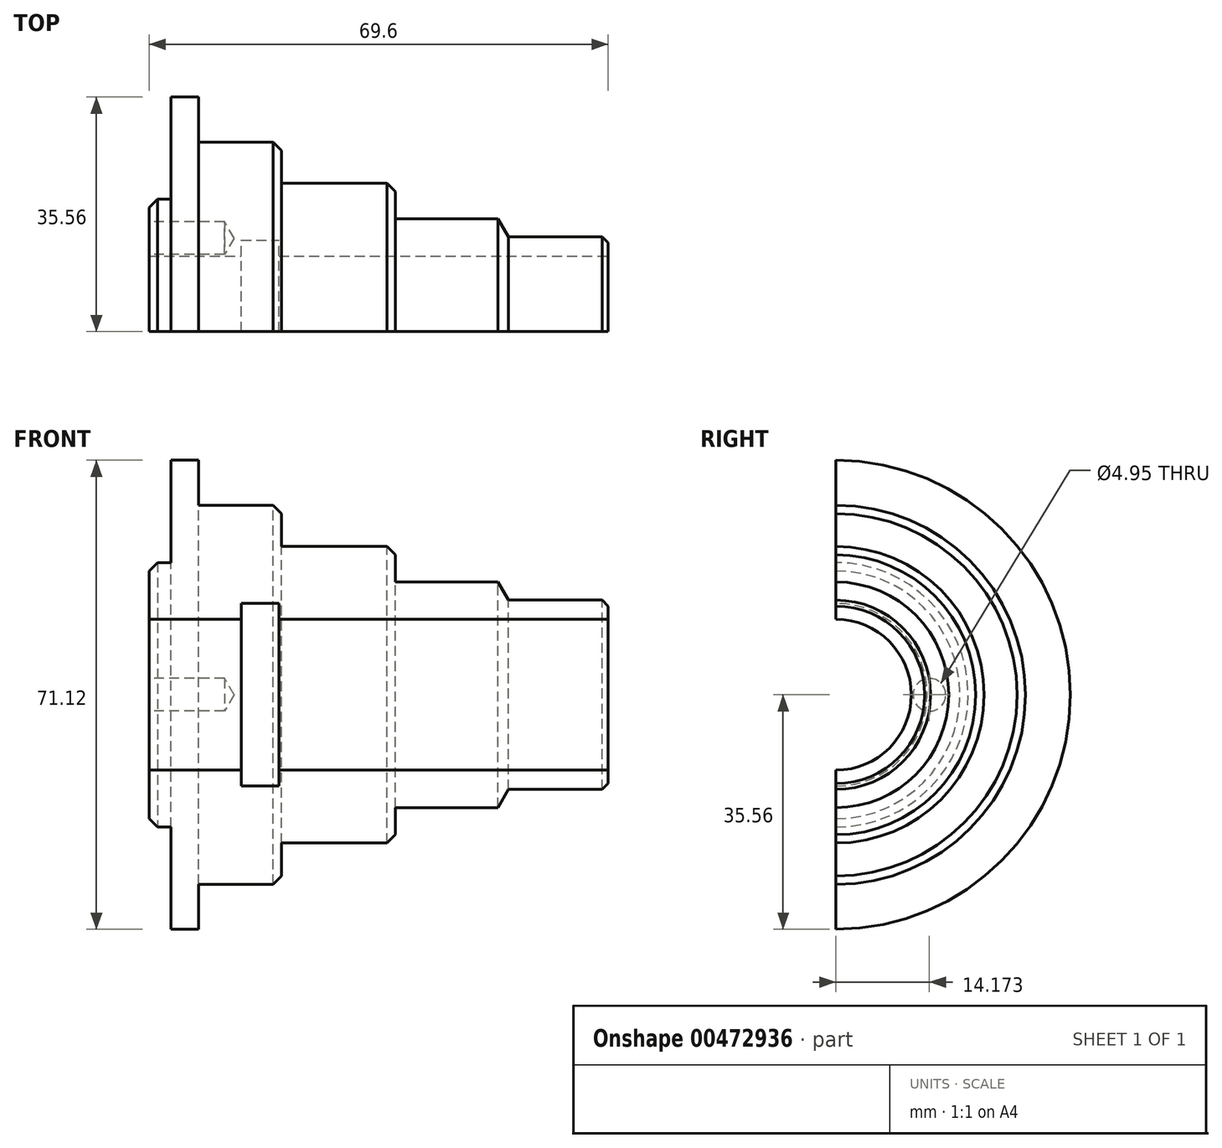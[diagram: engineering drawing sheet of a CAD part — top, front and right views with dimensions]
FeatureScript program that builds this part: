
annotation { "Feature Type Name" : "Feature", "Feature Type Description" : "" }
export const myFeature = defineFeature(function(context is Context, id is Id, definition is map)
    precondition{}
    {
        {
            var Q0;
            Q0=qCreatedBy(makeId("Front.planeOp"),FACE);
            var sketch = newSketch(context, id + "F0", { "sketchPlane" : qUnion([Q0])});
            skLineSegment(sketch, "E0", {"start": v(0, 0) * mm, "end": v(0, 11.43) * mm});
            skLineSegment(sketch, "E1", {"start": v(0, 11.43) * mm, "end": v(0, 13.45) * mm});
            skLineSegment(sketch, "E2", {"start": v(0, 13.45) * mm, "end": v(-0.9, 14.35) * mm});
            skLineSegment(sketch, "E3", {"start": v(-0.9, 14.35) * mm, "end": v(-15.12, 14.35) * mm});
            skLineSegment(sketch, "E4", {"start": v(0, 11.43) * mm, "end": v(-49.91, 11.43) * mm});
            skLineSegment(sketch, "E5", {"start": v(-15.12, 14.35) * mm, "end": v(-16.7, 17.1) * mm});
            skLineSegment(sketch, "E6", {"start": v(-16.7, 17.1) * mm, "end": v(-32.26, 17.1) * mm});
            skLineSegment(sketch, "E7", {"start": v(-32.26, 17.1) * mm, "end": v(-32.26, 22.48) * mm});
            skLineSegment(sketch, "E8", {"start": v(-32.26, 22.48) * mm, "end": v(-49.53, 22.48) * mm});
            skLineSegment(sketch, "E9", {"start": v(-49.53, 22.48) * mm, "end": v(-49.53, 28.74) * mm});
            skLineSegment(sketch, "E10", {"start": v(-49.53, 28.74) * mm, "end": v(-62.1, 28.74) * mm});
            skLineSegment(sketch, "E11", {"start": v(-62.1, 28.74) * mm, "end": v(-62.1, 35.56) * mm});
            skLineSegment(sketch, "E12", {"start": v(-62.1, 35.56) * mm, "end": v(-66.3, 35.56) * mm});
            skLineSegment(sketch, "E13", {"start": v(-66.3, 35.56) * mm, "end": v(-66.3, 20.05) * mm});
            skLineSegment(sketch, "E14", {"start": v(-66.3, 20.05) * mm, "end": v(-69.6, 20.05) * mm});
            skLineSegment(sketch, "E15", {"start": v(-69.6, 20.05) * mm, "end": v(-69.6, 11.43) * mm});
            skLineSegment(sketch, "E16", {"start": v(0, 0) * mm, "end": v(-69.06, 0) * mm});
            skLineSegment(sketch, "E17", {"start": v(-69.6, 11.43) * mm, "end": v(-55.63, 11.43) * mm});
            skLineSegment(sketch, "E18", {"start": v(-55.63, 11.43) * mm, "end": v(-55.63, 13.84) * mm});
            skLineSegment(sketch, "E19", {"start": v(-55.63, 13.84) * mm, "end": v(-49.91, 13.84) * mm});
            skLineSegment(sketch, "E20", {"start": v(-49.91, 13.84) * mm, "end": v(-49.91, 11.43) * mm});
            skLineSegment(sketch, "E21.trimOffspring", {"start": v(-55.63, 11.43) * mm, "end": v(-254, 11.43) * mm});
            skSolve(sketch);
        }
        {
            var Q0;
            Q0=makeQuery(id+"F0.imprint","IMPRINT",FACE,{"disambiguationData":[TD([[makeQuery(id+"F0.imprint","IMPRINT",EDGE,{"derivedFrom":sQuery(id+"F0.wireOp",EDGE,"E1")}),1.0]])]});
            var Q1;
            Q1=sQuery(id+"F0.wireOp",EDGE,"E16");
            revolve(context, id + "F1", {"entities" : qUnion([Q0]), "axis" : qUnion([Q1]), "revolveType" : RevolveType.FULL});
        }
        {
            var Q0;
            Q0=qCreatedBy(makeId("Front.planeOp"),FACE);
            var sketch = newSketch(context, id + "F2", { "sketchPlane" : qUnion([Q0])});
            skLineSegment(sketch, "E22.bottom", {"start": v(-76.46, 39.41) * mm, "end": v(0, 39.41) * mm});
            skLineSegment(sketch, "E22.top", {"start": v(-76.46, -39.22) * mm, "end": v(0, -39.22) * mm});
            skLineSegment(sketch, "E22.left", {"start": v(-76.46, 39.41) * mm, "end": v(-76.46, -39.22) * mm});
            skLineSegment(sketch, "E22.right", {"start": v(0, 39.41) * mm, "end": v(0, -39.22) * mm});
            skSolve(sketch);
        }
        {
            var Q0;
            Q0=makeQuery(id+"F2.imprint","IMPRINT",FACE,{"disambiguationData":[TD([[makeQuery(id+"F2.imprint","IMPRINT",EDGE,{"derivedFrom":sQuery(id+"F2.wireOp",EDGE,"E22.bottom")}),-1.0]])]});
            extrude(context, id + "F3", {"entities" : qUnion([Q0]), "operationType" : NewBodyOperationType.REMOVE, "endBound" : BoundingType.THROUGH_ALL, "depth" : 25.4 * mm});
        }
        {
            var Q0;
            Q0=makeQuery(id+"F1.opRevolve","SWEPT_EDGE",EDGE,{"disambiguationData":[OSD([sQuery(id+"F0.wireOp",EDGE,"E14"),sQuery(id+"F0.wireOp",EDGE,"E15")])]});
            var Q1;
            Q1=makeQuery(id+"F1.opRevolve","SWEPT_EDGE",EDGE,{"disambiguationData":[OSD([sQuery(id+"F0.wireOp",EDGE,"E9"),sQuery(id+"F0.wireOp",EDGE,"E10")])]});
            var Q2;
            Q2=makeQuery(id+"F1.opRevolve","SWEPT_EDGE",EDGE,{"disambiguationData":[OSD([sQuery(id+"F0.wireOp",EDGE,"E7"),sQuery(id+"F0.wireOp",EDGE,"E8")])]});
            chamfer(context, id + "F4", {"entities" : qUnion([Q0, Q1, Q2]), "width" : 1.27 * mm, "tangentPropagation" : true});
        }
        {
            var Q0;
            Q0=makeQuery(id+"F1.opRevolve","SWEPT_FACE",FACE,{"disambiguationData":[OSD([sQuery(id+"F0.wireOp",EDGE,"E15")])]});
            var sketch = newSketch(context, id + "F5", { "sketchPlane" : qUnion([Q0])});
            skPoint(sketch, "E23.endSnap0", {"position": v(-18.78, 0) * mm});
            skLineSegment(sketch, "E24", {"start": v(-11.43, 0) * mm, "end": v(-20.05, 0) * mm});
            skPoint(sketch, "E25", {"position": v(-14.17, 0) * mm});
            skSolve(sketch);
        }
        {
            var Q0;
            Q0=sQuery(id+"F5.wireOp",VERTEX,"E25");
            var Q1;
            Q1=makeQuery(id+"F1.opRevolve","SWEPT_BODY",BODY,{"disambiguationData":[OSD([sQuery(id+"F0.wireOp",EDGE,"E1"),sQuery(id+"F0.wireOp",EDGE,"E2"),sQuery(id+"F0.wireOp",EDGE,"E3"),sQuery(id+"F0.wireOp",EDGE,"E4"),sQuery(id+"F0.wireOp",EDGE,"E5"),sQuery(id+"F0.wireOp",EDGE,"E6"),sQuery(id+"F0.wireOp",EDGE,"E7"),sQuery(id+"F0.wireOp",EDGE,"E8"),sQuery(id+"F0.wireOp",EDGE,"E9"),sQuery(id+"F0.wireOp",EDGE,"E10"),sQuery(id+"F0.wireOp",EDGE,"E11"),sQuery(id+"F0.wireOp",EDGE,"E12"),sQuery(id+"F0.wireOp",EDGE,"E13"),sQuery(id+"F0.wireOp",EDGE,"E14"),sQuery(id+"F0.wireOp",EDGE,"E15"),sQuery(id+"F0.wireOp",EDGE,"E18"),sQuery(id+"F0.wireOp",EDGE,"E19"),sQuery(id+"F0.wireOp",EDGE,"E20"),sQuery(id+"F0.wireOp",EDGE,"E21.trimOffspring")])]});
            hole(context, id + "F6", {"style" : HoleStyle.SIMPLE, "endStyle" : HoleEndStyle.BLIND, "holeDiameter" : 4.95 * mm, "holeDepth" : 11.43 * mm, "isTappedThrough" : true, "tappedDepth" : 8.9 * mm, "tapClearance" : 3, "locations" : qUnion([Q0]), "scope" : qUnion([Q1])});
        }
    });
